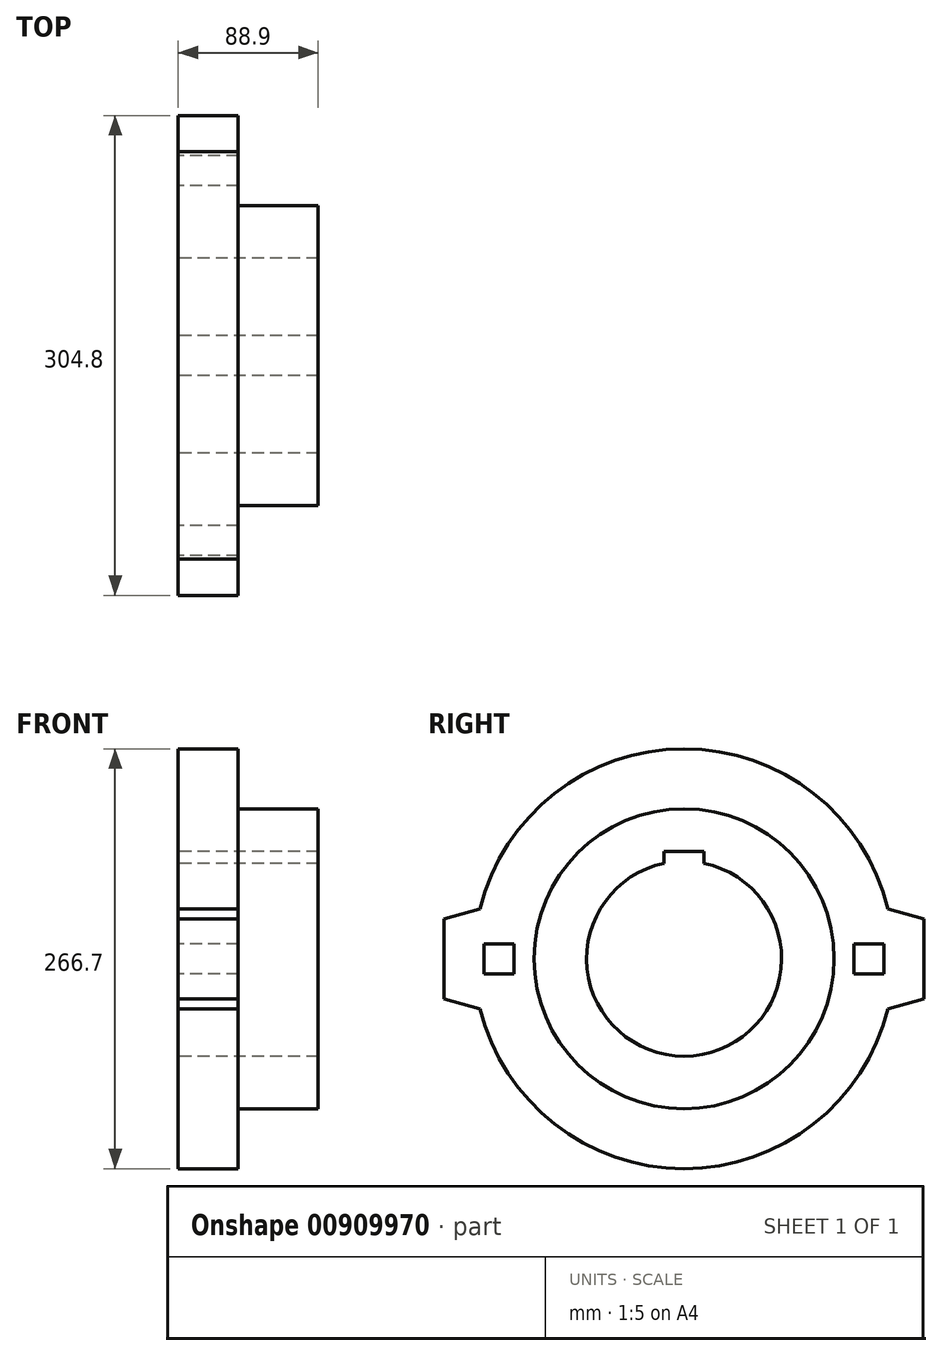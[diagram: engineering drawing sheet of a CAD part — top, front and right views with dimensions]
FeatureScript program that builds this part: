
annotation { "Feature Type Name" : "Feature", "Feature Type Description" : "" }
export const myFeature = defineFeature(function(context is Context, id is Id, definition is map)
    precondition{}
    {
        {
            var Q0;
            Q0=qCreatedBy(makeId("Right.planeOp"),FACE);
            var sketch = newSketch(context, id + "F0", { "sketchPlane" : qUnion([Q0])});
            skCircle(sketch, "E0", {"center": v(0, 0) * mm, "radius": 95.25 * mm});
            skArc(sketch, "E1", {"start": v(-129.52, -31.75) * mm, "mid": v(0, -133.35) * mm, "end": v(129.52, -31.75) * mm});
            skCircle(sketch, "E2", {"center": v(0, 0) * mm, "radius": 61.91 * mm});
            skLineSegment(sketch, "E3.bottom", {"start": v(-12.7, 68.26) * mm, "end": v(12.7, 68.26) * mm});
            skLineSegment(sketch, "E3.top", {"start": v(-12.7, 49.23) * mm, "end": v(12.7, 49.23) * mm});
            skLineSegment(sketch, "E3.left", {"start": v(-12.7, 68.26) * mm, "end": v(-12.7, 49.23) * mm});
            skLineSegment(sketch, "E3.right", {"start": v(12.7, 68.26) * mm, "end": v(12.7, 49.23) * mm});
            skLineSegment(sketch, "E4", {"start": v(0, 68.26) * mm, "end": v(0, 0) * mm, "construction": true});
            skLineSegment(sketch, "E5", {"start": v(-129.52, 31.75) * mm, "end": v(-152.4, 25.4) * mm});
            skLineSegment(sketch, "E6", {"start": v(-152.4, 25.4) * mm, "end": v(-152.4, -25.4) * mm});
            skLineSegment(sketch, "E7", {"start": v(-152.4, -25.4) * mm, "end": v(-129.52, -31.75) * mm});
            skLineSegment(sketch, "E8", {"start": v(129.52, -31.75) * mm, "end": v(152.4, -25.4) * mm});
            skLineSegment(sketch, "E9", {"start": v(152.4, -25.4) * mm, "end": v(152.4, 25.4) * mm});
            skLineSegment(sketch, "E10", {"start": v(152.4, 25.4) * mm, "end": v(129.52, 31.75) * mm});
            skLineSegment(sketch, "E11", {"start": v(-152.4, 0) * mm, "end": v(-107.95, 0) * mm, "construction": true});
            skArc(sketch, "E12.trimOffspring", {"start": v(129.52, 31.75) * mm, "mid": v(0, 133.35) * mm, "end": v(-129.52, 31.75) * mm});
            skLineSegment(sketch, "E13.bottom", {"start": v(-127, 9.52) * mm, "end": v(-107.95, 9.52) * mm});
            skLineSegment(sketch, "E13.top", {"start": v(-127, -9.53) * mm, "end": v(-107.95, -9.53) * mm});
            skLineSegment(sketch, "E13.left", {"start": v(-127, 9.53) * mm, "end": v(-127, -9.53) * mm});
            skLineSegment(sketch, "E13.right", {"start": v(-107.95, 9.52) * mm, "end": v(-107.95, 0) * mm});
            skLineSegment(sketch, "E14.bottom", {"start": v(107.95, 9.52) * mm, "end": v(127, 9.52) * mm});
            skLineSegment(sketch, "E14.top", {"start": v(107.95, -9.53) * mm, "end": v(127, -9.53) * mm});
            skLineSegment(sketch, "E14.left", {"start": v(107.95, 9.52) * mm, "end": v(107.95, 0) * mm});
            skLineSegment(sketch, "E14.right", {"start": v(127, 9.52) * mm, "end": v(127, -9.52) * mm});
            skPoint(sketch, "E15", {"position": v(-107.95, 0) * mm});
            skLineSegment(sketch, "E16", {"start": v(0, 0) * mm, "end": v(107.95, 0) * mm, "construction": true});
            skLineSegment(sketch, "E17", {"start": v(-107.95, 0) * mm, "end": v(-107.95, -9.52) * mm});
            skLineSegment(sketch, "E18", {"start": v(-107.95, 0) * mm, "end": v(0, 0) * mm, "construction": true});
            skLineSegment(sketch, "E19", {"start": v(107.95, 0) * mm, "end": v(107.95, -9.52) * mm});
            skLineSegment(sketch, "E20", {"start": v(107.95, 0) * mm, "end": v(152.4, 0) * mm, "construction": true});
            skSolve(sketch);
        }
        {
            var Q0;
            Q0=makeQuery(id+"F0.imprint","IMPRINT",FACE,{"disambiguationData":[TD([[makeQuery(id+"F0.imprint","IMPRINT",EDGE,{"derivedFrom":sQuery(id+"F0.wireOp",EDGE,"E0")}),1.0]])]});
            extrude(context, id + "F1", {"entities" : qUnion([Q0]), "depth" : 88.9 * mm, "offsetDistance" : 25 * mm});
        }
        {
            var Q0;
            Q0=makeQuery(id+"F0.imprint","IMPRINT",FACE,{"disambiguationData":[TD([[makeQuery(id+"F0.imprint","IMPRINT",EDGE,{"derivedFrom":sQuery(id+"F0.wireOp",EDGE,"E0")}),-1.0]])]});
            extrude(context, id + "F2", {"entities" : qUnion([Q0]), "operationType" : NewBodyOperationType.ADD, "depth" : 38.1 * mm, "offsetDistance" : 25 * mm});
        }
    });
